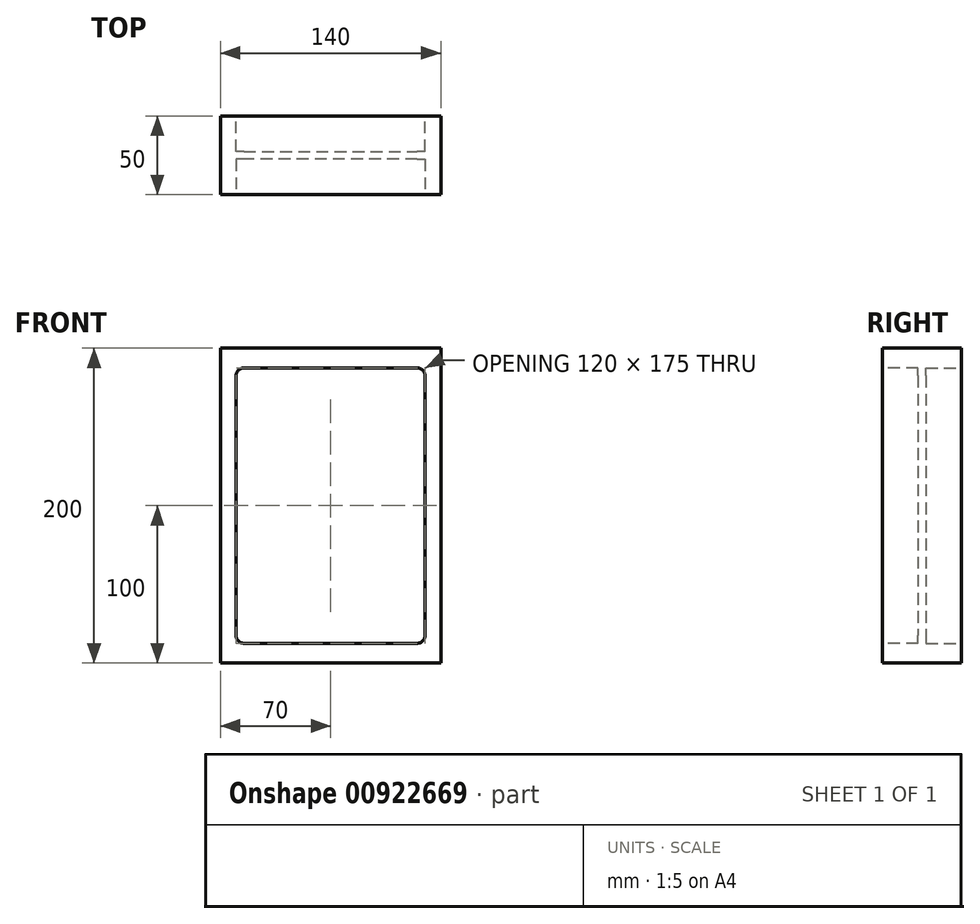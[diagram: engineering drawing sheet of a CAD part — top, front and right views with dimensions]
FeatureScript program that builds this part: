
annotation { "Feature Type Name" : "Feature", "Feature Type Description" : "" }
export const myFeature = defineFeature(function(context is Context, id is Id, definition is map)
    precondition{}
    {
        {
            var Q0;
            Q0=qCreatedBy(makeId("Front.planeOp"),FACE);
            var sketch = newSketch(context, id + "F0", { "sketchPlane" : qUnion([Q0])});
            skLineSegment(sketch, "E0.bottom", {"start": v(0, 0) * mm, "end": v(140, 0) * mm});
            skLineSegment(sketch, "E0.top", {"start": v(0, 200) * mm, "end": v(140, 200) * mm});
            skLineSegment(sketch, "E0.left", {"start": v(0, 0) * mm, "end": v(0, 200) * mm});
            skLineSegment(sketch, "E0.right", {"start": v(140, 0) * mm, "end": v(140, 200) * mm});
            skSolve(sketch);
        }
        {
            var Q0;
            Q0 = qSketchRegion(id + "F0", true);
            extrude(context, id + "F1", {"entities" : qUnion([Q0]), "depth" : 50 * mm, "offsetDistance" : 25 * mm});
        }
        {
            var Q0;
            Q0=makeQuery(id+"F1.opExtrude","CAP_FACE",FACE,{"disambiguationData":[OSD([sQuery(id+"F0.wireOp",EDGE,"E0.bottom"),sQuery(id+"F0.wireOp",EDGE,"E0.top"),sQuery(id+"F0.wireOp",EDGE,"E0.left"),sQuery(id+"F0.wireOp",EDGE,"E0.right")])],"isStart":false});
            var sketch = newSketch(context, id + "F2", { "sketchPlane" : qUnion([Q0])});
            skLineSegment(sketch, "E1.bottom", {"start": v(130, 187.5) * mm, "end": v(10, 187.5) * mm});
            skLineSegment(sketch, "E1.top", {"start": v(130, 12.5) * mm, "end": v(10, 12.5) * mm});
            skLineSegment(sketch, "E1.left", {"start": v(130, 187.5) * mm, "end": v(130, 12.5) * mm});
            skLineSegment(sketch, "E1.right", {"start": v(10, 187.5) * mm, "end": v(10, 12.5) * mm});
            skPoint(sketch, "E1.middle", {"position": v(70, 100) * mm});
            skPoint(sketch, "E1.middle.positionSnap0", {"position": v(70, 200) * mm});
            skPoint(sketch, "E1.middle.positionSnap1", {"position": v(0, 100) * mm});
            skPoint(sketch, "E1.centerSnap0", {"position": v(70, 200) * mm});
            skPoint(sketch, "E1.centerSnap1", {"position": v(0, 100) * mm});
            skSolve(sketch);
        }
        {
            var Q0;
            Q0 = qSketchRegion(id + "F2", true);
            extrude(context, id + "F3", {"entities" : qUnion([Q0]), "operationType" : NewBodyOperationType.REMOVE, "oppositeDirection" : true, "depth" : 22.5 * mm, "offsetDistance" : 25 * mm});
        }
        {
            var Q0;
            Q0=makeQuery(id+"F1.opExtrude","CAP_FACE",FACE,{"disambiguationData":[OSD([sQuery(id+"F0.wireOp",EDGE,"E0.bottom"),sQuery(id+"F0.wireOp",EDGE,"E0.top"),sQuery(id+"F0.wireOp",EDGE,"E0.left"),sQuery(id+"F0.wireOp",EDGE,"E0.right")])],"isStart":true});
            var sketch = newSketch(context, id + "F4", { "sketchPlane" : qUnion([Q0])});
            skLineSegment(sketch, "E2.bottom", {"start": v(-10, 187.5) * mm, "end": v(-130, 187.5) * mm});
            skLineSegment(sketch, "E2.top", {"start": v(-10, 12.5) * mm, "end": v(-130, 12.5) * mm});
            skLineSegment(sketch, "E2.left", {"start": v(-10, 187.5) * mm, "end": v(-10, 12.5) * mm});
            skLineSegment(sketch, "E2.right", {"start": v(-130, 187.5) * mm, "end": v(-130, 12.5) * mm});
            skPoint(sketch, "E2.middle", {"position": v(-70, 100) * mm});
            skPoint(sketch, "E2.middle.positionSnap0", {"position": v(-70, 200) * mm});
            skPoint(sketch, "E2.middle.positionSnap1", {"position": v(-140, 100) * mm});
            skPoint(sketch, "E2.centerSnap0", {"position": v(-70, 200) * mm});
            skPoint(sketch, "E2.centerSnap1", {"position": v(-140, 100) * mm});
            skSolve(sketch);
        }
        {
            var Q0;
            Q0=makeQuery(id+"F4.imprint","IMPRINT",FACE,{"disambiguationData":[TD([[makeQuery(id+"F4.imprint","IMPRINT",EDGE,{"derivedFrom":sQuery(id+"F4.wireOp",EDGE,"E2.bottom")}),1.0]])]});
            extrude(context, id + "F5", {"entities" : qUnion([Q0]), "operationType" : NewBodyOperationType.REMOVE, "oppositeDirection" : true, "depth" : 22.5 * mm, "offsetDistance" : 25 * mm});
        }
        {
            var Q0;
            Q0=makeQuery(id+"F3.boolean.opBoolean","COPY",EDGE,{"derivedFrom":makeQuery(id+"F3.opExtrude","SWEPT_EDGE",EDGE,{"disambiguationData":[OSD([sQuery(id+"F2.wireOp",EDGE,"E1.bottom"),sQuery(id+"F2.wireOp",EDGE,"E1.left")])]})});
            var Q1;
            Q1=makeQuery(id+"F3.boolean.opBoolean","COPY",EDGE,{"derivedFrom":makeQuery(id+"F3.opExtrude","SWEPT_EDGE",EDGE,{"disambiguationData":[OSD([sQuery(id+"F2.wireOp",EDGE,"E1.bottom"),sQuery(id+"F2.wireOp",EDGE,"E1.right")])]})});
            var Q2;
            Q2=makeQuery(id+"F3.boolean.opBoolean","COPY",EDGE,{"derivedFrom":makeQuery(id+"F3.opExtrude","SWEPT_EDGE",EDGE,{"disambiguationData":[OSD([sQuery(id+"F2.wireOp",EDGE,"E1.top"),sQuery(id+"F2.wireOp",EDGE,"E1.right")])]})});
            var Q3;
            Q3=makeQuery(id+"F3.boolean.opBoolean","COPY",EDGE,{"derivedFrom":makeQuery(id+"F3.opExtrude","SWEPT_EDGE",EDGE,{"disambiguationData":[OSD([sQuery(id+"F2.wireOp",EDGE,"E1.top"),sQuery(id+"F2.wireOp",EDGE,"E1.left")])]})});
            var Q4;
            Q4=makeQuery(id+"F5.boolean.opBoolean","COPY",EDGE,{"derivedFrom":makeQuery(id+"F5.opExtrude","SWEPT_EDGE",EDGE,{"disambiguationData":[OSD([sQuery(id+"F4.wireOp",EDGE,"E2.bottom"),sQuery(id+"F4.wireOp",EDGE,"E2.right")])]})});
            var Q5;
            Q5=makeQuery(id+"F5.boolean.opBoolean","COPY",EDGE,{"derivedFrom":makeQuery(id+"F5.opExtrude","SWEPT_EDGE",EDGE,{"disambiguationData":[OSD([sQuery(id+"F4.wireOp",EDGE,"E2.bottom"),sQuery(id+"F4.wireOp",EDGE,"E2.left")])]})});
            var Q6;
            Q6=makeQuery(id+"F5.boolean.opBoolean","COPY",EDGE,{"derivedFrom":makeQuery(id+"F5.opExtrude","SWEPT_EDGE",EDGE,{"disambiguationData":[OSD([sQuery(id+"F4.wireOp",EDGE,"E2.top"),sQuery(id+"F4.wireOp",EDGE,"E2.left")])]})});
            var Q7;
            Q7=makeQuery(id+"F5.boolean.opBoolean","COPY",EDGE,{"derivedFrom":makeQuery(id+"F5.opExtrude","SWEPT_EDGE",EDGE,{"disambiguationData":[OSD([sQuery(id+"F4.wireOp",EDGE,"E2.top"),sQuery(id+"F4.wireOp",EDGE,"E2.right")])]})});
            fillet(context, id + "F6", {"entities" : qUnion([Q0, Q1, Q2, Q3, Q4, Q5, Q6, Q7]), "radius" : 5 * mm, "tangentPropagation" : true, "allowEdgeOverflow" : false});
        }
    });
